# Revit family: QF_FESTIVE_ACDH_cat_ACDH15
name_source: partatom
category: Specialty Equipment
units: mm (PartAtom-declared; Revit-internal decimal feet)

## family parameters
Always vertical = Yes
Cut with Voids When Loaded = No
Part Type = Normal
Room Calculation Point = No
Round Connector Dimension = Use Diameter
Shared = No
Work Plane-Based = No

## types (1)
- ACDH15
    Apparent Power = 1078 VA
    Center Post = No
    Conn Conduit = Yes
    Cradle 1 = No
    Cradle 2 = Yes
    Cycle = 50 Hz
    Default Elevation = 0 mm  [stored 0 ft]
    Depth = 830 mm  [stored 2.7231 ft]
    Description = AVON HI: CHILLED DROP-IN
    Elec Conn Connection Height = 0 mm  [stored 0 ft]
    Elec Conn RI Height = 0 mm  [stored 0 ft]
    FL Amps = 5 A
    Foodservice Equipment Identifier = Yes
    Height = 520 mm
    Identify Quantity as Lot = Yes
    Length = 1530 mm  [stored 5.01969 ft]
    Manufacturer = FESTIVE
    Max Overcurrent Protection = 0 A
    Min Ckt Ampacity = 0 A
    Model = ACDH15
    Number of Poles = 1
    Phase = 1
    Volts = 220 V
    Watts = 1078 W
    Weight in Pounds = 0

note: [stored X ft] marks values corroborated as IEEE doubles in the binary element streams (Revit-internal decimal feet)

## geometry (parser evidence)
native form markers: Sweep x9
no freeform markers — native parametric forms only
